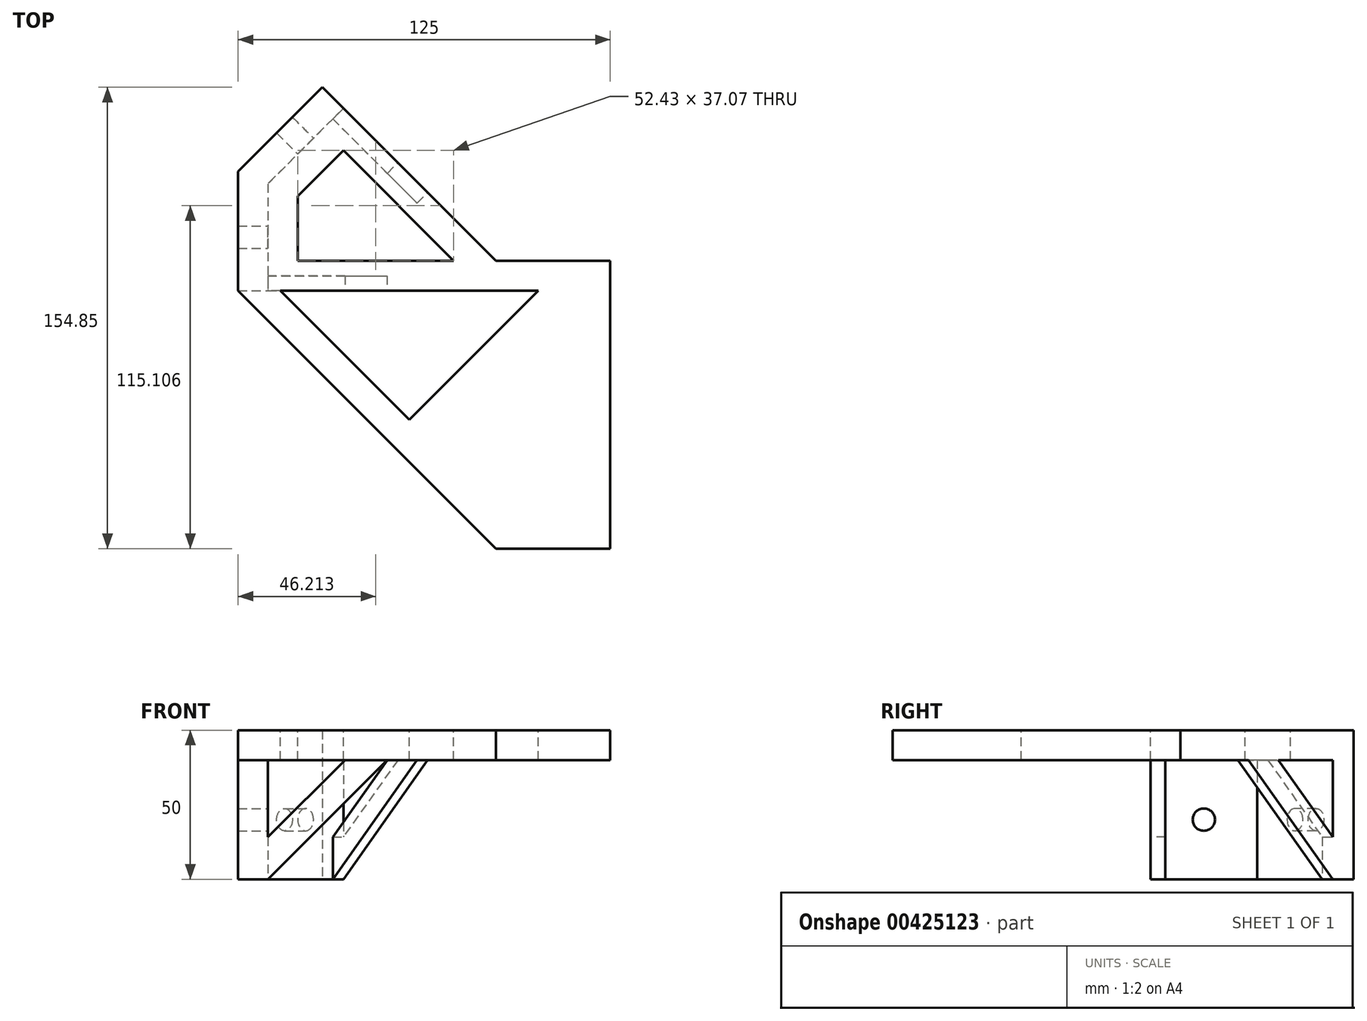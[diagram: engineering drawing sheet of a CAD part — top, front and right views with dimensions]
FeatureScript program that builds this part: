
annotation { "Feature Type Name" : "Feature", "Feature Type Description" : "" }
export const myFeature = defineFeature(function(context is Context, id is Id, definition is map)
    precondition{}
    {
        {
            var Q0;
            Q0=qCreatedBy(makeId("Top.planeOp"),FACE);
            var sketch = newSketch(context, id + "F0", { "sketchPlane" : qUnion([Q0])});
            skLineSegment(sketch, "E0", {"start": v(0, 0) * mm, "end": v(0, 40) * mm});
            skLineSegment(sketch, "E1", {"start": v(0, 40) * mm, "end": v(28.28, 68.28) * mm});
            skLineSegment(sketch, "E2", {"start": v(28.28, 68.28) * mm, "end": v(35.36, 61.21) * mm});
            skLineSegment(sketch, "E3", {"start": v(35.36, 61.21) * mm, "end": v(10, 35.86) * mm});
            skLineSegment(sketch, "E4", {"start": v(10, 35.86) * mm, "end": v(10, 0) * mm});
            skLineSegment(sketch, "E5", {"start": v(10, 0) * mm, "end": v(0, 0) * mm});
            skSolve(sketch);
        }
        {
            var Q0;
            Q0=makeQuery(id+"F0.imprint","IMPRINT",FACE,{"disambiguationData":[TD([[makeQuery(id+"F0.imprint","IMPRINT",EDGE,{"derivedFrom":sQuery(id+"F0.wireOp",EDGE,"E0")}),-1.0]])]});
            extrude(context, id + "F1", {"entities" : qUnion([Q0]), "depth" : 50 * mm});
        }
        {
            var Q0;
            Q0=makeQuery(id+"F1.opExtrude","CAP_FACE",FACE,{"disambiguationData":[OSD([sQuery(id+"F0.wireOp",EDGE,"E0"),sQuery(id+"F0.wireOp",EDGE,"E1"),sQuery(id+"F0.wireOp",EDGE,"E2"),sQuery(id+"F0.wireOp",EDGE,"E3"),sQuery(id+"F0.wireOp",EDGE,"E4"),sQuery(id+"F0.wireOp",EDGE,"E5")])],"isStart":false});
            var sketch = newSketch(context, id + "F2", { "sketchPlane" : qUnion([Q0])});
            skLineSegment(sketch, "E6.0", {"start": v(0, 40) * mm, "end": v(28.28, 68.28) * mm});
            skLineSegment(sketch, "E7.0", {"start": v(0, 0) * mm, "end": v(0, 40) * mm});
            skLineSegment(sketch, "E8", {"start": v(0, 0) * mm, "end": v(125, 0) * mm});
            skLineSegment(sketch, "E9", {"start": v(125, 0) * mm, "end": v(125, 10) * mm});
            skLineSegment(sketch, "E10", {"start": v(125, 10) * mm, "end": v(86.57, 10) * mm});
            skLineSegment(sketch, "E11", {"start": v(28.28, 68.28) * mm, "end": v(86.57, 10) * mm});
            skLineSegment(sketch, "E12", {"start": v(72.43, 10) * mm, "end": v(20, 10) * mm});
            skLineSegment(sketch, "E13", {"start": v(20, 10) * mm, "end": v(20, 31.72) * mm});
            skLineSegment(sketch, "E14", {"start": v(20, 31.72) * mm, "end": v(35.36, 47.07) * mm});
            skLineSegment(sketch, "E15", {"start": v(35.36, 47.07) * mm, "end": v(72.43, 10) * mm});
            skSolve(sketch);
        }
        {
            var Q0;
            {var subQ3=sQuery(id+"F2.wireOp",EDGE,"E9");Q0=makeQuery(id+"F2.imprint","IMPRINT",FACE,{"disambiguationData":[TD([[makeQuery(id+"F2.imprint","IMPRINT",EDGE,{"derivedFrom":subQ3}),1.0]])]});}
            extrude(context, id + "F3", {"entities" : qUnion([Q0]), "operationType" : NewBodyOperationType.ADD, "oppositeDirection" : true, "depth" : 10 * mm});
        }
        {
            var Q0;
            Q0=makeQuery(id+"F1.opExtrude","SWEPT_FACE",FACE,{"disambiguationData":[OSD([sQuery(id+"F0.wireOp",EDGE,"E3")])]});
            var sketch = newSketch(context, id + "F4", { "sketchPlane" : qUnion([Q0])});
            skCircle(sketch, "E16", {"center": v(50.36, 20) * mm, "radius": 3.75 * mm});
            skPoint(sketch, "E16.centerSnap0", {"position": v(50.36, 0) * mm});
            skPoint(sketch, "E16.centerSnap1", {"position": v(68.28, 20) * mm});
            skSolve(sketch);
        }
        {
            var Q0;
            Q0=makeQuery(id+"F1.opExtrude","SWEPT_FACE",FACE,{"disambiguationData":[OSD([sQuery(id+"F0.wireOp",EDGE,"E4")])]});
            var sketch = newSketch(context, id + "F5", { "sketchPlane" : qUnion([Q0])});
            skCircle(sketch, "E17", {"center": v(17.93, 20) * mm, "radius": 3.75 * mm});
            skPoint(sketch, "E17.centerSnap0", {"position": v(17.93, 0) * mm});
            skPoint(sketch, "E17.centerSnap1", {"position": v(0, 20) * mm});
            skSolve(sketch);
        }
        {
            var Q0;
            Q0=makeQuery(id+"F5.imprint","IMPRINT",FACE,{"disambiguationData":[TD([[makeQuery(id+"F5.imprint","IMPRINT",EDGE,{"derivedFrom":sQuery(id+"F5.wireOp",EDGE,"E17")}),1.0]])]});
            extrude(context, id + "F6", {"entities" : qUnion([Q0]), "operationType" : NewBodyOperationType.REMOVE, "endBound" : BoundingType.THROUGH_ALL, "oppositeDirection" : true, "depth" : 25 * mm});
        }
        {
            var Q0;
            Q0=makeQuery(id+"F4.imprint","IMPRINT",FACE,{"disambiguationData":[TD([[makeQuery(id+"F4.imprint","IMPRINT",EDGE,{"derivedFrom":sQuery(id+"F4.wireOp",EDGE,"E16")}),1.0]])]});
            var Q1;
            Q1=sQuery(id+"F4.wireOp",EDGE,"E16");
            extrude(context, id + "F7", {"entities" : qUnion([Q0]), "operationType" : NewBodyOperationType.REMOVE, "surfaceEntities" : qUnion([Q1]), "endBound" : BoundingType.THROUGH_ALL, "oppositeDirection" : true, "depth" : 25 * mm});
        }
        {
            var Q0;
            Q0=makeQuery(id+"F3.boolean.opBoolean","MERGE",FACE,{"derivedFrom":[makeQuery(id+"F1.opExtrude","SWEPT_FACE",FACE,{"disambiguationData":[OSD([sQuery(id+"F0.wireOp",EDGE,"E5")])]}),makeQuery(id+"F3.opExtrude","SWEPT_FACE",FACE,{"disambiguationData":[OSD([sQuery(id+"F2.wireOp",EDGE,"E8")])]})]});
            var sketch = newSketch(context, id + "F8", { "sketchPlane" : qUnion([Q0])});
            skLineSegment(sketch, "E18", {"start": v(10, 0) * mm, "end": v(50, 40) * mm});
            skLineSegment(sketch, "E19", {"start": v(50, 40) * mm, "end": v(35.86, 40) * mm});
            skLineSegment(sketch, "E20", {"start": v(35.86, 40) * mm, "end": v(10, 14.14) * mm});
            skLineSegment(sketch, "E21", {"start": v(10, 14.14) * mm, "end": v(10, 0) * mm});
            skSolve(sketch);
        }
        {
            var Q0;
            Q0=makeQuery(id+"F8.imprint","IMPRINT",FACE,{"disambiguationData":[TD([[makeQuery(id+"F8.imprint","IMPRINT",EDGE,{"derivedFrom":sQuery(id+"F8.wireOp",EDGE,"E18")}),1.0]])]});
            extrude(context, id + "F9", {"entities" : qUnion([Q0]), "operationType" : NewBodyOperationType.ADD, "oppositeDirection" : true, "depth" : 5 * mm});
        }
        {
            var Q0;
            Q0=makeQuery(id+"F3.boolean.opBoolean","MERGE",FACE,{"derivedFrom":[makeQuery(id+"F1.opExtrude","SWEPT_FACE",FACE,{"disambiguationData":[OSD([sQuery(id+"F0.wireOp",EDGE,"E2")])]}),makeQuery(id+"F3.opExtrude","SWEPT_FACE",FACE,{"disambiguationData":[OSD([sQuery(id+"F2.wireOp",EDGE,"E11")])]})]});
            var sketch = newSketch(context, id + "F10", { "sketchPlane" : qUnion([Q0])});
            skLineSegment(sketch, "E22", {"start": v(18.28, 0) * mm, "end": v(-21.72, 40) * mm});
            skLineSegment(sketch, "E23", {"start": v(-7.57, 40) * mm, "end": v(18.28, 14.14) * mm});
            skLineSegment(sketch, "E24", {"start": v(18.28, 0) * mm, "end": v(18.28, 14.14) * mm});
            skLineSegment(sketch, "E25", {"start": v(-7.57, 40) * mm, "end": v(-21.72, 40) * mm});
            skSolve(sketch);
        }
        {
            var Q0;
            Q0 = qSketchRegion(id + "F10", true);
            extrude(context, id + "F11", {"entities" : qUnion([Q0]), "operationType" : NewBodyOperationType.ADD, "oppositeDirection" : true, "depth" : 5 * mm});
        }
        {
            var Q0;
            {var subQ0=sQuery(id+"F0.wireOp",EDGE,"E4");var subQ1=sQuery(id+"F0.wireOp",EDGE,"E3");Q0=makeQuery(id+"F3.boolean.opBoolean","MERGE",FACE,{"derivedFrom":[makeQuery(id+"F1.opExtrude","CAP_FACE",FACE,{"disambiguationData":[OSD([sQuery(id+"F0.wireOp",EDGE,"E0"),sQuery(id+"F0.wireOp",EDGE,"E1"),sQuery(id+"F0.wireOp",EDGE,"E2"),subQ1,subQ0,sQuery(id+"F0.wireOp",EDGE,"E5")])],"isStart":false}),makeQuery(id+"F3.opExtrude","CAP_FACE",FACE,{"disambiguationData":[OSD([subQ1,subQ0,sQuery(id+"F2.wireOp",EDGE,"E8"),sQuery(id+"F2.wireOp",EDGE,"E9"),sQuery(id+"F2.wireOp",EDGE,"E10"),sQuery(id+"F2.wireOp",EDGE,"E11"),sQuery(id+"F2.wireOp",EDGE,"E12"),sQuery(id+"F2.wireOp",EDGE,"E13"),sQuery(id+"F2.wireOp",EDGE,"E14"),sQuery(id+"F2.wireOp",EDGE,"E15")])],"isStart":true})]});}
            var sketch = newSketch(context, id + "F12", { "sketchPlane" : qUnion([Q0])});
            skLineSegment(sketch, "E26", {"start": v(0, 0) * mm, "end": v(86.57, -86.57) * mm});
            skLineSegment(sketch, "E27", {"start": v(86.57, -86.57) * mm, "end": v(125, -86.57) * mm});
            skLineSegment(sketch, "E28", {"start": v(125, -86.57) * mm, "end": v(125, -76.57) * mm});
            skLineSegment(sketch, "E29", {"start": v(115, -76.57) * mm, "end": v(90.71, -76.57) * mm});
            skLineSegment(sketch, "E30", {"start": v(90.71, -76.57) * mm, "end": v(64.57, -50.43) * mm});
            skLineSegment(sketch, "E31", {"start": v(14.14, 0) * mm, "end": v(0, 0) * mm});
            skLineSegment(sketch, "E32", {"start": v(125, 0) * mm, "end": v(125, -76.57) * mm});
            skLineSegment(sketch, "E33", {"start": v(115, 0) * mm, "end": v(115, -76.57) * mm});
            skLineSegment(sketch, "E34", {"start": v(100.86, 0) * mm, "end": v(57.5, -43.36) * mm});
            skLineSegment(sketch, "E35", {"start": v(64.57, -50.43) * mm, "end": v(115, 0) * mm});
            skLineSegment(sketch, "E36", {"start": v(115, 0) * mm, "end": v(100.86, 0) * mm});
            skLineSegment(sketch, "E37", {"start": v(125, 0) * mm, "end": v(115, 0) * mm});
            skLineSegment(sketch, "E38.trimOffspring", {"start": v(57.5, -43.36) * mm, "end": v(14.14, 0) * mm});
            skSolve(sketch);
        }
        {
            var Q0;
            Q0 = qSketchRegion(id + "F12", true);
            var Q1;
            Q1=makeQuery(id+"F3.opExtrude","CAP_FACE",FACE,{"disambiguationData":[OSD([sQuery(id+"F0.wireOp",EDGE,"E3"),sQuery(id+"F0.wireOp",EDGE,"E4"),sQuery(id+"F2.wireOp",EDGE,"E8"),sQuery(id+"F2.wireOp",EDGE,"E9"),sQuery(id+"F2.wireOp",EDGE,"E10"),sQuery(id+"F2.wireOp",EDGE,"E11"),sQuery(id+"F2.wireOp",EDGE,"E12"),sQuery(id+"F2.wireOp",EDGE,"E13"),sQuery(id+"F2.wireOp",EDGE,"E14"),sQuery(id+"F2.wireOp",EDGE,"E15")])],"isStart":false});
            extrude(context, id + "F13", {"entities" : qUnion([Q0]), "operationType" : NewBodyOperationType.ADD, "endBound" : BoundingType.UP_TO_SURFACE, "oppositeDirection" : true, "endBoundEntityFace" : qUnion([Q1]), "depth" : 25 * mm});
        }
    });
